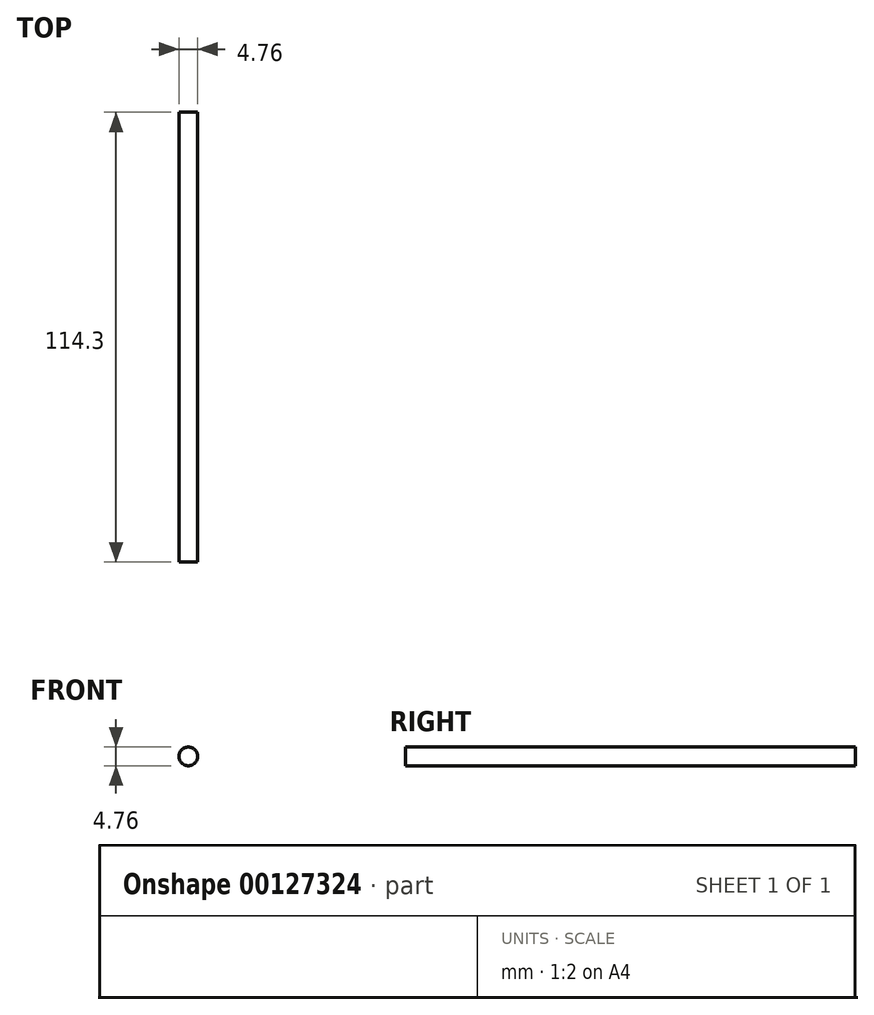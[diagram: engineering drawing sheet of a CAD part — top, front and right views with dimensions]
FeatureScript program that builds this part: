
annotation { "Feature Type Name" : "Feature", "Feature Type Description" : "" }
export const myFeature = defineFeature(function(context is Context, id is Id, definition is map)
    precondition{}
    {
        {
            var Q0;
            Q0=qCreatedBy(makeId("Front.planeOp"),FACE);
            var sketch = newSketch(context, id + "F0", { "sketchPlane" : qUnion([Q0])});
            skCircle(sketch, "E0", {"center": v(0, 0) * mm, "radius": 2.38 * mm});
            skSolve(sketch);
        }
        {
            var Q0;
            Q0 = qSketchRegion(id + "F0", true);
            extrude(context, id + "F1", {"entities" : qUnion([Q0]), "oppositeDirection" : true, "depth" : 114.3 * mm});
        }
    });
